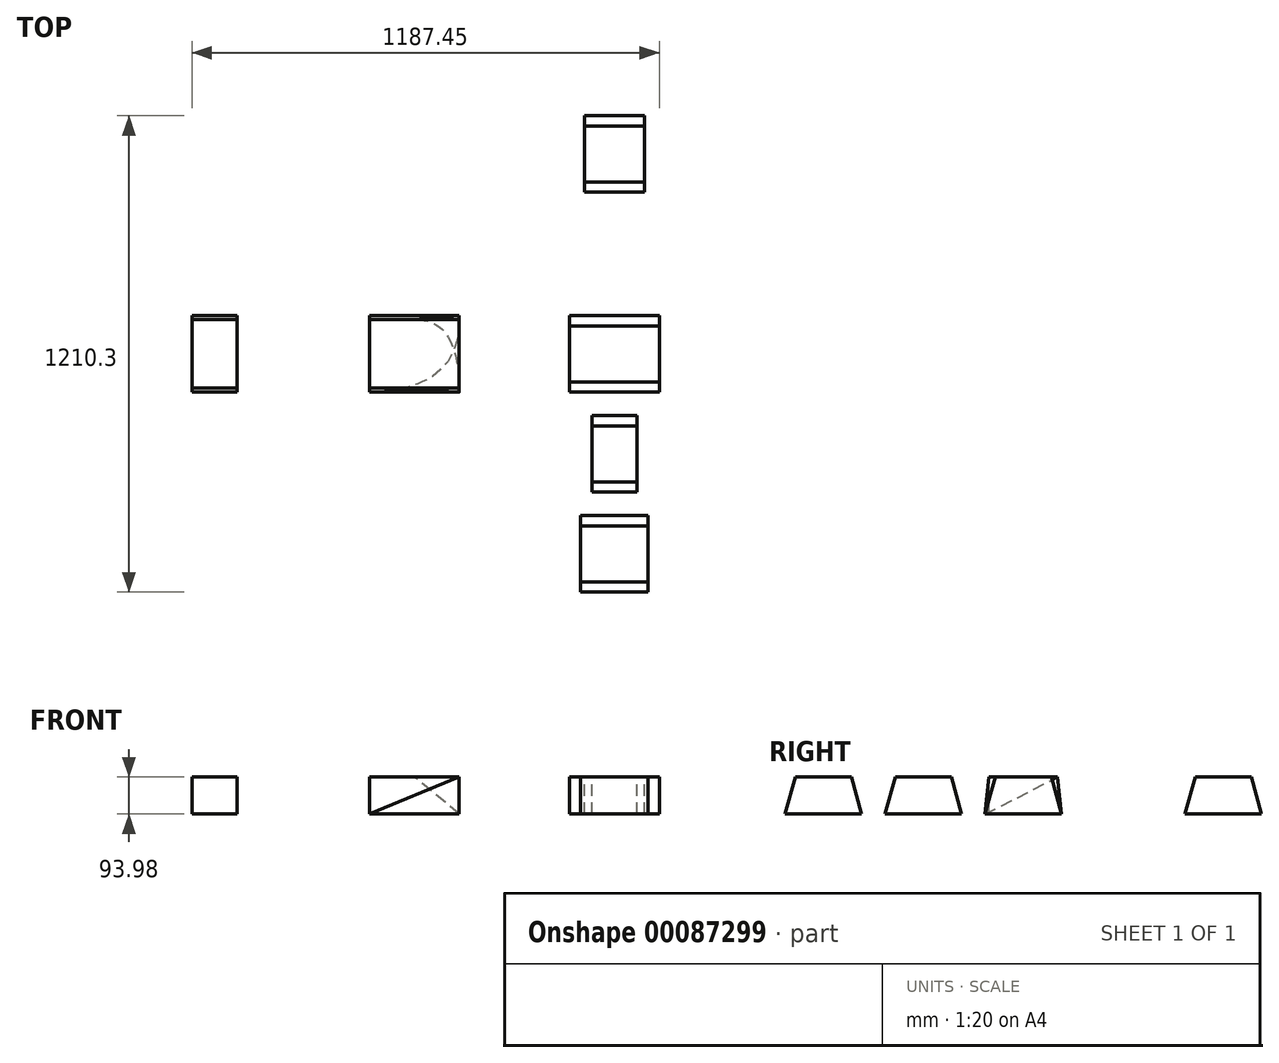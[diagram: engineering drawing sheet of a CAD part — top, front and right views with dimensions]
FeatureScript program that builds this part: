
annotation { "Feature Type Name" : "Feature", "Feature Type Description" : "" }
export const myFeature = defineFeature(function(context is Context, id is Id, definition is map)
    precondition{}
    {
        {
            var Q0;
            Q0=qCreatedBy(makeId("Top.planeOp"),FACE);
            var sketch = newSketch(context, id + "F0", { "sketchPlane" : qUnion([Q0]), "disableImprinting" : false});
            skLineSegment(sketch, "E0.bottom", {"start": v(114.3, -97.16) * mm, "end": v(-114.3, -97.16) * mm});
            skLineSegment(sketch, "E0.top", {"start": v(114.3, 97.16) * mm, "end": v(-114.3, 97.16) * mm});
            skLineSegment(sketch, "E0.left", {"start": v(114.3, -97.16) * mm, "end": v(114.3, 97.16) * mm});
            skLineSegment(sketch, "E0.right", {"start": v(-114.3, -97.16) * mm, "end": v(-114.3, 97.16) * mm});
            skPoint(sketch, "E0.middle", {"position": v(0, 0) * mm});
            skLineSegment(sketch, "E1", {"start": v(0, 97.16) * mm, "end": v(0, -97.16) * mm, "construction": true});
            skLineSegment(sketch, "E2.bottom", {"start": v(-57.15, -156.84) * mm, "end": v(57.15, -156.84) * mm});
            skLineSegment(sketch, "E2.top", {"start": v(-57.15, -351.16) * mm, "end": v(57.15, -351.16) * mm});
            skLineSegment(sketch, "E2.left", {"start": v(-57.15, -156.84) * mm, "end": v(-57.15, -351.16) * mm});
            skLineSegment(sketch, "E2.right", {"start": v(57.15, -156.84) * mm, "end": v(57.15, -351.16) * mm});
            skPoint(sketch, "E2.middle", {"position": v(0, -254) * mm});
            skLineSegment(sketch, "E3", {"start": v(0, 0) * mm, "end": v(-114.3, 0) * mm, "construction": true});
            skLineSegment(sketch, "E4", {"start": v(-57.15, 0) * mm, "end": v(-57.15, -97.16) * mm, "construction": true});
            skLineSegment(sketch, "E5", {"start": v(-57.15, -48.58) * mm, "end": v(114.3, -48.58) * mm, "construction": true});
            skLineSegment(sketch, "E6.bottom", {"start": v(-85.72, -410.84) * mm, "end": v(85.73, -410.84) * mm});
            skLineSegment(sketch, "E6.top", {"start": v(-85.73, -605.15) * mm, "end": v(85.73, -605.15) * mm});
            skLineSegment(sketch, "E6.left", {"start": v(-85.72, -410.84) * mm, "end": v(-85.73, -605.15) * mm});
            skLineSegment(sketch, "E6.right", {"start": v(85.73, -410.84) * mm, "end": v(85.73, -605.15) * mm});
            skPoint(sketch, "E6.middle", {"position": v(0, -508) * mm});
            skPoint(sketch, "E6.middle.positionSnap0", {"position": v(0, -351.16) * mm});
            skPoint(sketch, "E6.centerSnap0", {"position": v(0, -351.16) * mm});
            skLineSegment(sketch, "E7", {"start": v(-38.1, 97.16) * mm, "end": v(-38.1, -97.16) * mm, "construction": true});
            skLineSegment(sketch, "E8", {"start": v(38.1, 97.16) * mm, "end": v(38.1, -97.16) * mm, "construction": true});
            skLineSegment(sketch, "E9", {"start": v(-114.3, 38.22) * mm, "end": v(-38.1, 38.22) * mm, "construction": true});
            skLineSegment(sketch, "E10", {"start": v(-38.1, 38.22) * mm, "end": v(38.1, 38.22) * mm, "construction": true});
            skLineSegment(sketch, "E11", {"start": v(38.1, 38.22) * mm, "end": v(114.3, 38.22) * mm, "construction": true});
            skLineSegment(sketch, "E12.bottom", {"start": v(76.2, 410.85) * mm, "end": v(0, 410.85) * mm});
            skLineSegment(sketch, "E12.top", {"start": v(76.2, 605.16) * mm, "end": v(-76.2, 605.16) * mm});
            skLineSegment(sketch, "E12.left", {"start": v(76.2, 410.85) * mm, "end": v(76.2, 605.16) * mm});
            skLineSegment(sketch, "E12.right", {"start": v(-76.2, 410.85) * mm, "end": v(-76.2, 605.16) * mm});
            skPoint(sketch, "E12.middle", {"position": v(0, 508) * mm});
            skLineSegment(sketch, "E13", {"start": v(0, 605.16) * mm, "end": v(0, 410.85) * mm, "construction": true});
            skLineSegment(sketch, "E14", {"start": v(0, 410.85) * mm, "end": v(-76.2, 410.85) * mm});
            skLineSegment(sketch, "E15.bottom", {"start": v(-622.3, 97.15) * mm, "end": v(-393.7, 97.15) * mm});
            skLineSegment(sketch, "E15.top", {"start": v(-622.3, -97.15) * mm, "end": v(-393.7, -97.16) * mm});
            skLineSegment(sketch, "E15.left", {"start": v(-622.3, 97.15) * mm, "end": v(-622.3, 87) * mm});
            skLineSegment(sketch, "E15.right", {"start": v(-393.7, 97.16) * mm, "end": v(-393.7, -97.15) * mm});
            skPoint(sketch, "E15.middle", {"position": v(-508, 0) * mm});
            skLineSegment(sketch, "E16", {"start": v(-622.3, -87) * mm, "end": v(-622.3, -87) * mm});
            skLineSegment(sketch, "E17", {"start": v(-622.3, 87) * mm, "end": v(-393.7, 87) * mm, "construction": true});
            skLineSegment(sketch, "E18", {"start": v(-622.3, 87) * mm, "end": v(-622.3, -87) * mm});
            skLineSegment(sketch, "E19", {"start": v(-622.3, -87) * mm, "end": v(-393.7, -87) * mm, "construction": true});
            skLineSegment(sketch, "E20", {"start": v(-622.3, -87) * mm, "end": v(-622.3, -92.07) * mm});
            skLineSegment(sketch, "E21", {"start": v(-622.3, -87) * mm, "end": v(-622.3, -97.16) * mm});
            skLineSegment(sketch, "E22", {"start": v(-508, 97.15) * mm, "end": v(-508, -97.15) * mm, "construction": true});
            skLineSegment(sketch, "E23", {"start": v(-622.3, 0) * mm, "end": v(-508, 0) * mm, "construction": true});
            skLineSegment(sketch, "E24.bottom", {"start": v(-958.85, 97.16) * mm, "end": v(-1073.15, 97.16) * mm});
            skLineSegment(sketch, "E24.top", {"start": v(-958.85, -97.15) * mm, "end": v(-1073.15, -97.15) * mm});
            skLineSegment(sketch, "E24.left", {"start": v(-958.85, 97.16) * mm, "end": v(-958.85, -97.15) * mm});
            skLineSegment(sketch, "E24.right", {"start": v(-1073.15, 97.16) * mm, "end": v(-1073.15, -97.15) * mm});
            skPoint(sketch, "E24.middle", {"position": v(-1016, 0) * mm});
            skSolve(sketch);
        }
        {
            var Q0;
            Q0=makeQuery(id+"F0.imprint","IMPRINT",FACE,{"disambiguationData":[TD([[makeQuery(id+"F0.imprint","IMPRINT",EDGE,{"derivedFrom":sQuery(id+"F0.wireOp",EDGE,"E0.bottom")}),-1.0]])]});
            cPlane(context, id + "F1", {"entities" : qUnion([Q0]), "cplaneType" : CPlaneType.OFFSET, "offset" : 93.98 * mm, "width" : 152.4 * mm, "height" : 152.4 * mm});
        }
        {
            var Q0;
            Q0=qCreatedBy(id+"F1.planeOp",FACE);
            var sketch = newSketch(context, id + "F2", { "sketchPlane" : qUnion([Q0]), "disableImprinting" : false});
            skLineSegment(sketch, "E25.bottom", {"start": v(-114.3, 70.87) * mm, "end": v(114.3, 70.87) * mm});
            skLineSegment(sketch, "E25.top", {"start": v(-114.3, -70.87) * mm, "end": v(114.3, -70.87) * mm});
            skLineSegment(sketch, "E25.left", {"start": v(-114.3, 70.87) * mm, "end": v(-114.3, -70.87) * mm});
            skLineSegment(sketch, "E25.right", {"start": v(114.3, 70.87) * mm, "end": v(114.3, -70.87) * mm});
            skPoint(sketch, "E25.middle", {"position": v(0, 0) * mm});
            skLineSegment(sketch, "E26.bottom", {"start": v(-57.15, -183.13) * mm, "end": v(57.15, -183.13) * mm});
            skLineSegment(sketch, "E26.top", {"start": v(-57.15, -324.87) * mm, "end": v(57.15, -324.87) * mm});
            skLineSegment(sketch, "E26.left", {"start": v(-57.15, -183.13) * mm, "end": v(-57.15, -324.87) * mm});
            skLineSegment(sketch, "E26.right", {"start": v(57.15, -183.13) * mm, "end": v(57.15, -324.87) * mm});
            skPoint(sketch, "E26.middle", {"position": v(0, -254) * mm});
            skLineSegment(sketch, "E27", {"start": v(0, 70.87) * mm, "end": v(0, -70.87) * mm, "construction": true});
            skLineSegment(sketch, "E28", {"start": v(-114.3, 0) * mm, "end": v(0, 0) * mm, "construction": true});
            skLineSegment(sketch, "E29", {"start": v(-57.15, 0) * mm, "end": v(-57.15, -70.87) * mm, "construction": true});
            skLineSegment(sketch, "E30", {"start": v(-57.15, -35.43) * mm, "end": v(114.3, -35.43) * mm, "construction": true});
            skLineSegment(sketch, "E31.bottom", {"start": v(-85.72, -437.13) * mm, "end": v(85.73, -437.13) * mm});
            skLineSegment(sketch, "E31.top", {"start": v(-85.73, -578.87) * mm, "end": v(85.73, -578.87) * mm});
            skLineSegment(sketch, "E31.left", {"start": v(-85.72, -437.13) * mm, "end": v(-85.73, -578.87) * mm});
            skLineSegment(sketch, "E31.right", {"start": v(85.73, -437.13) * mm, "end": v(85.73, -578.87) * mm});
            skPoint(sketch, "E31.middle", {"position": v(0, -508) * mm});
            skLineSegment(sketch, "E32", {"start": v(-38.1, 70.87) * mm, "end": v(-38.1, -70.87) * mm, "construction": true});
            skLineSegment(sketch, "E33", {"start": v(38.1, 70.87) * mm, "end": v(38.1, -70.87) * mm, "construction": true});
            skLineSegment(sketch, "E34", {"start": v(-114.3, 29.5) * mm, "end": v(-38.1, 29.5) * mm, "construction": true});
            skLineSegment(sketch, "E35", {"start": v(-38.1, 29.5) * mm, "end": v(38.1, 29.5) * mm, "construction": true});
            skLineSegment(sketch, "E36", {"start": v(38.1, 29.5) * mm, "end": v(114.3, 29.5) * mm, "construction": true});
            skLineSegment(sketch, "E37.bottom", {"start": v(76.2, 437.13) * mm, "end": v(0, 437.13) * mm});
            skLineSegment(sketch, "E37.top", {"start": v(76.2, 578.87) * mm, "end": v(-76.2, 578.87) * mm});
            skLineSegment(sketch, "E37.left", {"start": v(76.2, 437.13) * mm, "end": v(76.2, 578.87) * mm});
            skLineSegment(sketch, "E37.right", {"start": v(-76.2, 437.13) * mm, "end": v(-76.2, 578.87) * mm});
            skPoint(sketch, "E37.middle", {"position": v(0, 508) * mm});
            skLineSegment(sketch, "E38", {"start": v(0, 578.87) * mm, "end": v(0, 437.13) * mm, "construction": true});
            skLineSegment(sketch, "E39", {"start": v(0, 437.13) * mm, "end": v(-76.2, 437.13) * mm});
            skLineSegment(sketch, "E40.bottom", {"start": v(-622.3, -87) * mm, "end": v(-393.7, -87) * mm});
            skLineSegment(sketch, "E40.top", {"start": v(-622.3, 87) * mm, "end": v(-393.7, 87) * mm});
            skLineSegment(sketch, "E40.left", {"start": v(-622.3, -87) * mm, "end": v(-622.3, 87) * mm});
            skLineSegment(sketch, "E40.right", {"start": v(-393.7, -87) * mm, "end": v(-393.7, 87) * mm});
            skPoint(sketch, "E40.middle", {"position": v(-508, 0) * mm});
            skPoint(sketch, "E40.middle.positionSnap0", {"position": v(-38.1, 0) * mm});
            skPoint(sketch, "E40.centerSnap0", {"position": v(-38.1, 0) * mm});
            skLineSegment(sketch, "E41.bottom", {"start": v(-1073.15, 87) * mm, "end": v(-958.85, 87) * mm});
            skLineSegment(sketch, "E41.top", {"start": v(-1073.15, -87) * mm, "end": v(-958.85, -87) * mm});
            skLineSegment(sketch, "E41.left", {"start": v(-1073.15, 87) * mm, "end": v(-1073.15, -87) * mm});
            skLineSegment(sketch, "E41.right", {"start": v(-958.85, 87) * mm, "end": v(-958.85, -87) * mm});
            skPoint(sketch, "E41.middle", {"position": v(-1016, 0) * mm});
            skSolve(sketch);
        }
        {
            var Q0;
            Q0=makeQuery(id+"F0.imprint","IMPRINT",FACE,{"disambiguationData":[TD([[makeQuery(id+"F0.imprint","IMPRINT",EDGE,{"derivedFrom":sQuery(id+"F0.wireOp",EDGE,"E0.bottom")}),-1.0]])]});
            var Q1;
            Q1=makeQuery(id+"F2.imprint","IMPRINT",FACE,{"disambiguationData":[TD([[makeQuery(id+"F2.imprint","IMPRINT",EDGE,{"derivedFrom":sQuery(id+"F2.wireOp",EDGE,"E25.bottom")}),-1.0]])]});
            loft(context, id + "F3", {"sheetProfilesArray" : [{ "sheetProfileEntities" : qUnion([Q0]) }, { "sheetProfileEntities" : qUnion([Q1]) }], "trimGuidesByProfiles" : true});
        }
        {
            var Q0;
            Q0=makeQuery(id+"F0.imprint","IMPRINT",FACE,{"disambiguationData":[TD([[makeQuery(id+"F0.imprint","IMPRINT",EDGE,{"derivedFrom":sQuery(id+"F0.wireOp",EDGE,"E2.bottom")}),-1.0]])]});
            var Q1;
            Q1=makeQuery(id+"F2.imprint","IMPRINT",FACE,{"disambiguationData":[TD([[makeQuery(id+"F2.imprint","IMPRINT",EDGE,{"derivedFrom":sQuery(id+"F2.wireOp",EDGE,"E26.bottom")}),-1.0]])]});
            loft(context, id + "F4", {"sheetProfilesArray" : [{ "sheetProfileEntities" : qUnion([Q0]) }, { "sheetProfileEntities" : qUnion([Q1]) }]});
        }
        {
            var Q0;
            Q0=makeQuery(id+"F0.imprint","IMPRINT",FACE,{"disambiguationData":[TD([[makeQuery(id+"F0.imprint","IMPRINT",EDGE,{"derivedFrom":sQuery(id+"F0.wireOp",EDGE,"E6.bottom")}),-1.0]])]});
            var Q1;
            Q1=makeQuery(id+"F2.imprint","IMPRINT",FACE,{"disambiguationData":[TD([[makeQuery(id+"F2.imprint","IMPRINT",EDGE,{"derivedFrom":sQuery(id+"F2.wireOp",EDGE,"E31.bottom")}),-1.0]])]});
            loft(context, id + "F5", {"sheetProfilesArray" : [{ "sheetProfileEntities" : qUnion([Q0]) }, { "sheetProfileEntities" : qUnion([Q1]) }]});
        }
        {
            var Q0;
            Q0=makeQuery(id+"F0.imprint","IMPRINT",FACE,{"disambiguationData":[TD([[makeQuery(id+"F0.imprint","IMPRINT",EDGE,{"derivedFrom":sQuery(id+"F0.wireOp",EDGE,"E12.bottom")}),-1.0]])]});
            var Q1;
            Q1=makeQuery(id+"F2.imprint","IMPRINT",FACE,{"disambiguationData":[TD([[makeQuery(id+"F2.imprint","IMPRINT",EDGE,{"derivedFrom":sQuery(id+"F2.wireOp",EDGE,"E37.bottom")}),-1.0]])]});
            loft(context, id + "F6", {"sheetProfilesArray" : [{ "sheetProfileEntities" : qUnion([Q0]) }, { "sheetProfileEntities" : qUnion([Q1]) }]});
        }
        {
            var Q0;
            Q0=makeQuery(id+"F0.imprint","IMPRINT",FACE,{"disambiguationData":[TD([[makeQuery(id+"F0.imprint","IMPRINT",EDGE,{"derivedFrom":sQuery(id+"F0.wireOp",EDGE,"E15.bottom")}),-1.0]])]});
            var Q1;
            Q1=makeQuery(id+"F2.imprint","IMPRINT",FACE,{"disambiguationData":[TD([[makeQuery(id+"F2.imprint","IMPRINT",EDGE,{"derivedFrom":sQuery(id+"F2.wireOp",EDGE,"E40.bottom")}),1.0]])]});
            loft(context, id + "F7", {"sheetProfilesArray" : [{ "sheetProfileEntities" : qUnion([Q0]) }, { "sheetProfileEntities" : qUnion([Q1]) }]});
        }
        {
            var Q0;
            Q0=makeQuery(id+"F0.imprint","IMPRINT",FACE,{"disambiguationData":[TD([[makeQuery(id+"F0.imprint","IMPRINT",EDGE,{"derivedFrom":sQuery(id+"F0.wireOp",EDGE,"E24.bottom")}),1.0]])]});
            var Q1;
            Q1=makeQuery(id+"F2.imprint","IMPRINT",FACE,{"disambiguationData":[TD([[makeQuery(id+"F2.imprint","IMPRINT",EDGE,{"derivedFrom":sQuery(id+"F2.wireOp",EDGE,"E41.bottom")}),-1.0]])]});
            loft(context, id + "F8", {"sheetProfilesArray" : [{ "sheetProfileEntities" : qUnion([Q0]) }, { "sheetProfileEntities" : qUnion([Q1]) }]});
        }
    });
